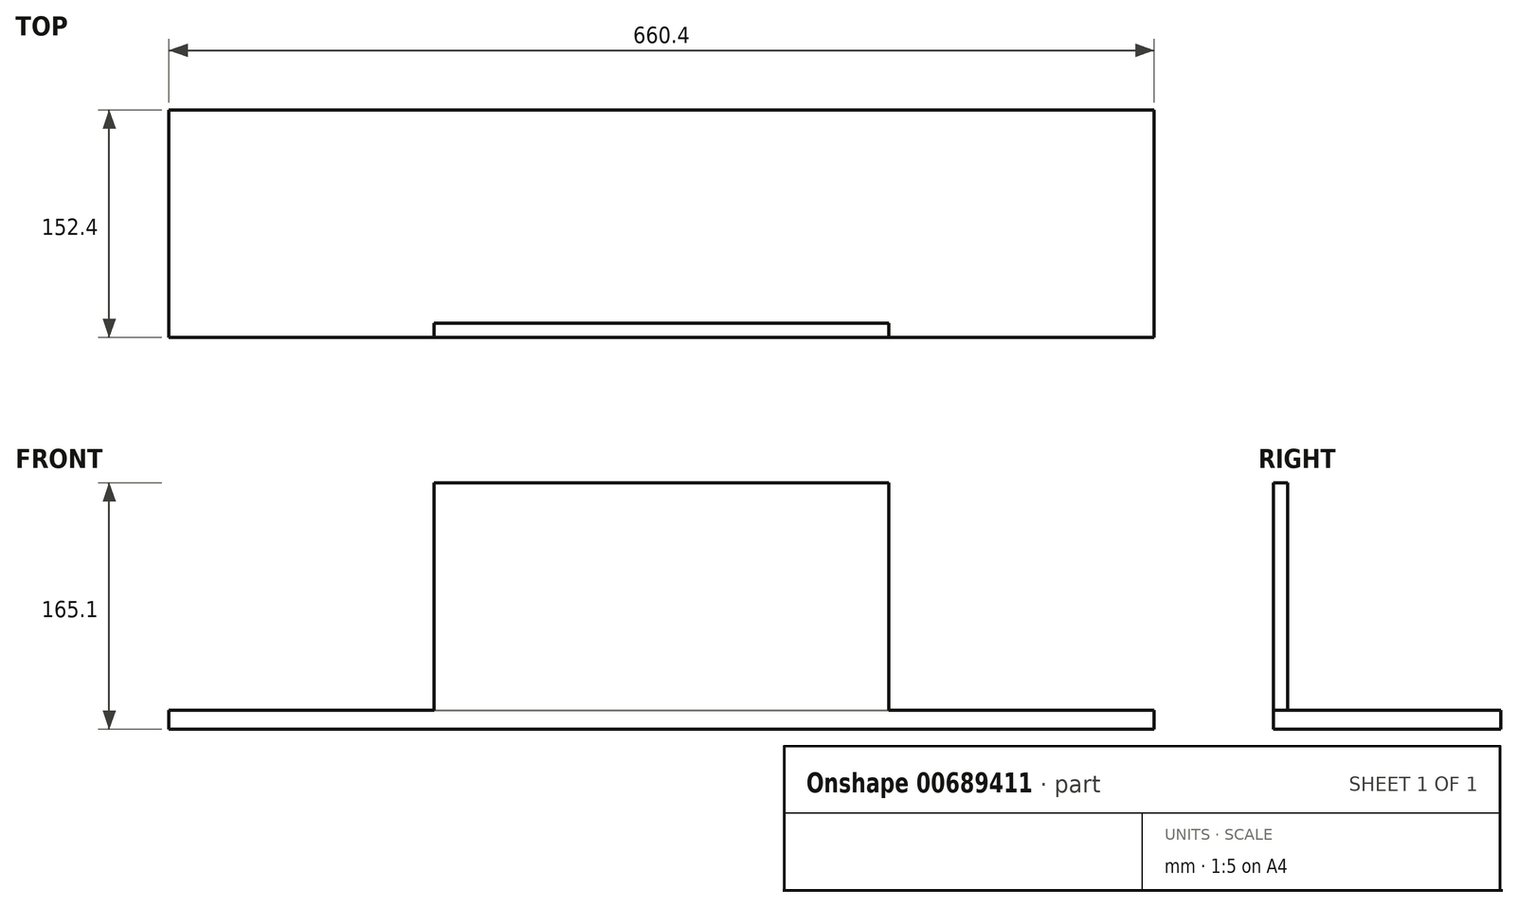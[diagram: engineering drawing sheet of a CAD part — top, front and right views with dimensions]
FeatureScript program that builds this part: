
annotation { "Feature Type Name" : "Feature", "Feature Type Description" : "" }
export const myFeature = defineFeature(function(context is Context, id is Id, definition is map)
    precondition{}
    {
        {
            var Q0;
            Q0=qCreatedBy(makeId("Top.planeOp"),FACE);
            var sketch = newSketch(context, id + "F0", { "sketchPlane" : qUnion([Q0])});
            skLineSegment(sketch, "E0.bottom", {"start": v(-330.2, 76.2) * mm, "end": v(330.2, 76.2) * mm});
            skLineSegment(sketch, "E0.top", {"start": v(-330.2, -76.2) * mm, "end": v(330.2, -76.2) * mm});
            skLineSegment(sketch, "E0.left", {"start": v(-330.2, 76.2) * mm, "end": v(-330.2, -76.2) * mm});
            skLineSegment(sketch, "E0.right", {"start": v(330.2, 76.2) * mm, "end": v(330.2, -76.2) * mm});
            skPoint(sketch, "E0.middle", {"position": v(0, 0) * mm});
            skSolve(sketch);
        }
        {
            var Q0;
            Q0=makeQuery(id+"F0.imprint","IMPRINT",FACE,{"disambiguationData":[TD([[makeQuery(id+"F0.imprint","IMPRINT",EDGE,{"derivedFrom":sQuery(id+"F0.wireOp",EDGE,"E0.bottom")}),-1.0]])]});
            extrude(context, id + "F1", {"entities" : qUnion([Q0]), "depth" : 12.7 * mm, "offsetDistance" : 25.4 * mm});
        }
        {
            var Q0;
            Q0=makeQuery(id+"F1.opExtrude","SWEPT_FACE",FACE,{"disambiguationData":[OSD([sQuery(id+"F0.wireOp",EDGE,"E0.top")])]});
            var sketch = newSketch(context, id + "F2", { "sketchPlane" : qUnion([Q0])});
            skLineSegment(sketch, "E1.bottom", {"start": v(-152.4, 165.1) * mm, "end": v(152.4, 165.1) * mm});
            skLineSegment(sketch, "E1.top", {"start": v(-152.4, 12.7) * mm, "end": v(152.4, 12.7) * mm});
            skLineSegment(sketch, "E1.left", {"start": v(-152.4, 165.1) * mm, "end": v(-152.4, 12.7) * mm});
            skLineSegment(sketch, "E1.right", {"start": v(152.4, 165.1) * mm, "end": v(152.4, 12.7) * mm});
            skPoint(sketch, "E1.middle", {"position": v(0, 88.9) * mm});
            skSolve(sketch);
        }
        {
            var Q0;
            Q0=makeQuery(id+"F2.imprint","IMPRINT",FACE,{"disambiguationData":[TD([[makeQuery(id+"F2.imprint","IMPRINT",EDGE,{"derivedFrom":sQuery(id+"F2.wireOp",EDGE,"E1.bottom")}),-1.0]])]});
            extrude(context, id + "F3", {"entities" : qUnion([Q0]), "operationType" : NewBodyOperationType.ADD, "oppositeDirection" : true, "depth" : 9.52 * mm, "offsetDistance" : 25.4 * mm});
        }
    });
